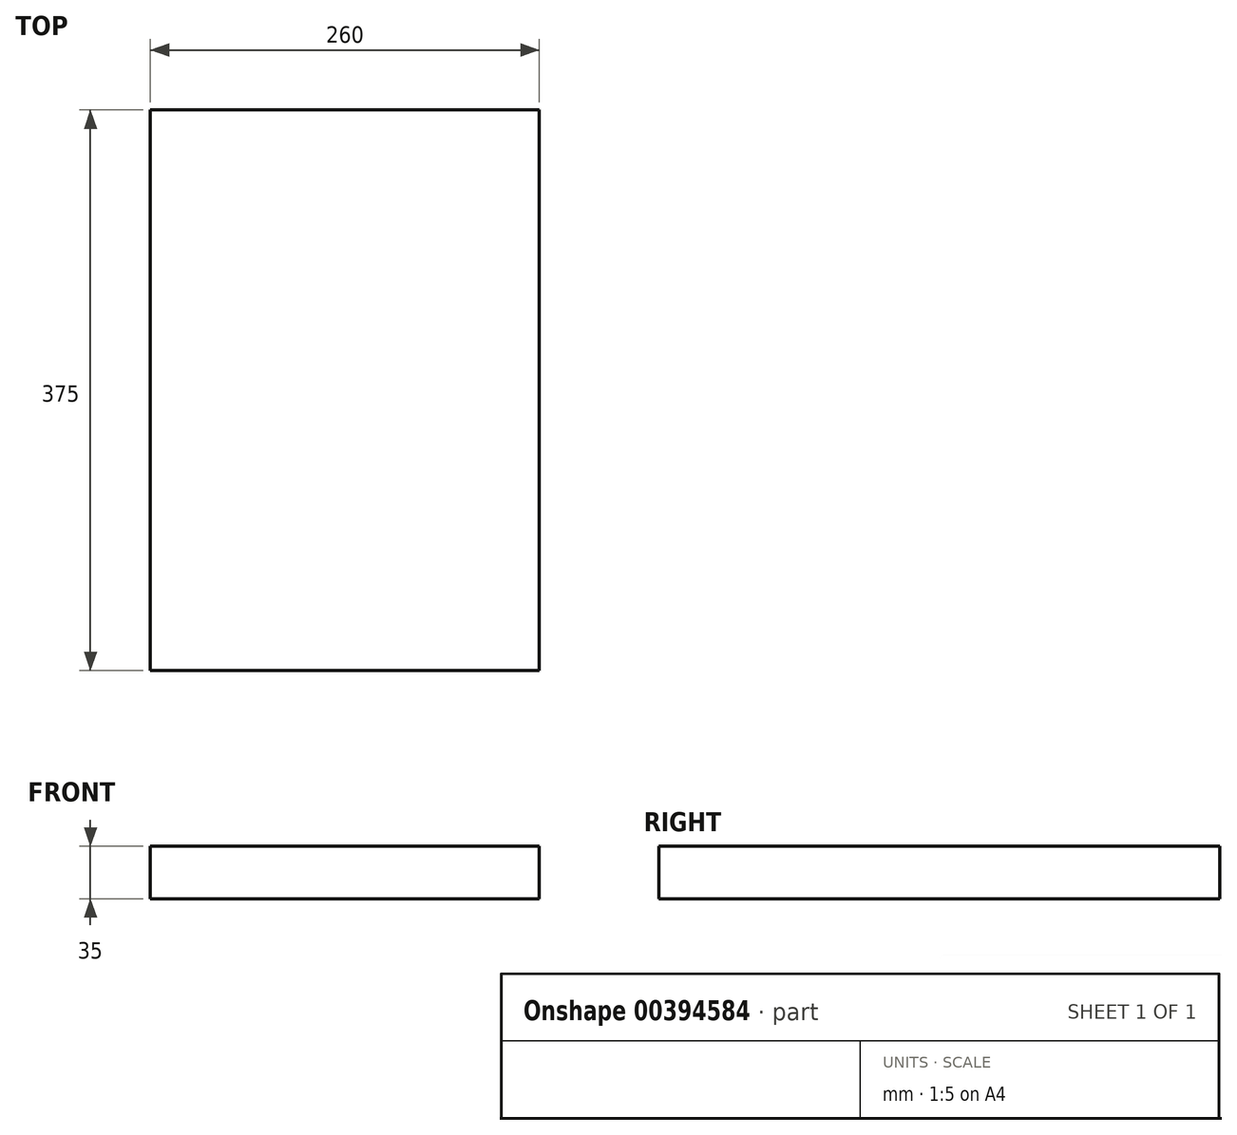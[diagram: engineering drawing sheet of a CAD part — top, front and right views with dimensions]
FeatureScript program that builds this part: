
annotation { "Feature Type Name" : "Feature", "Feature Type Description" : "" }
export const myFeature = defineFeature(function(context is Context, id is Id, definition is map)
    precondition{}
    {
        {
            var Q0;
            Q0=qCreatedBy(makeId("Top.planeOp"),FACE);
            var sketch = newSketch(context, id + "F0", { "sketchPlane" : qUnion([Q0])});
            skLineSegment(sketch, "E0.bottom", {"start": v(130, 187.5) * mm, "end": v(-130, 187.5) * mm});
            skLineSegment(sketch, "E0.top", {"start": v(130, -187.5) * mm, "end": v(-130, -187.5) * mm});
            skLineSegment(sketch, "E0.left", {"start": v(130, 187.5) * mm, "end": v(130, -187.5) * mm});
            skLineSegment(sketch, "E0.right", {"start": v(-130, 187.5) * mm, "end": v(-130, -187.5) * mm});
            skPoint(sketch, "E0.middle", {"position": v(0, 0) * mm});
            skSolve(sketch);
        }
        {
            var Q0;
            Q0=makeQuery(id+"F0.imprint","IMPRINT",FACE,{"disambiguationData":[TD([[makeQuery(id+"F0.imprint","IMPRINT",EDGE,{"derivedFrom":sQuery(id+"F0.wireOp",EDGE,"E0.bottom")}),1.0]])]});
            extrude(context, id + "F1", {"entities" : qUnion([Q0]), "depth" : 35 * mm});
        }
    });
